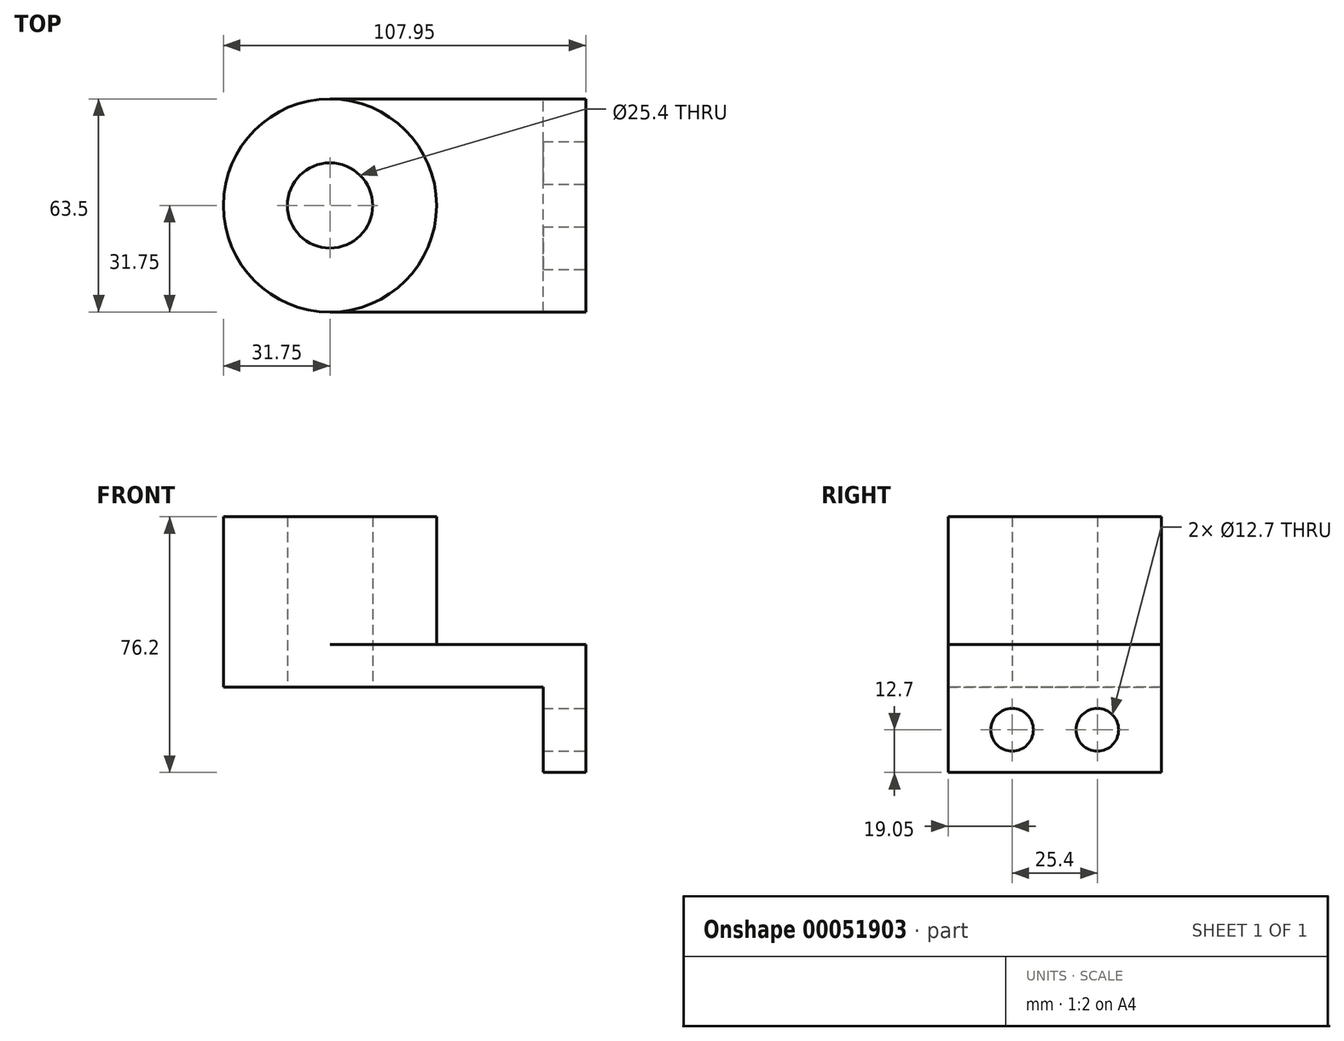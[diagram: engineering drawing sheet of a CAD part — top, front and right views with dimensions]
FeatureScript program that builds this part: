
annotation { "Feature Type Name" : "Feature", "Feature Type Description" : "" }
export const myFeature = defineFeature(function(context is Context, id is Id, definition is map)
    precondition{}
    {
        {
            var Q0;
            Q0=qCreatedBy(makeId("Top.planeOp"),FACE);
            var sketch = newSketch(context, id + "F0", { "sketchPlane" : qUnion([Q0])});
            skLineSegment(sketch, "E0.rect.bottom", {"start": v(38.1, -31.75) * mm, "end": v(-38.1, -31.75) * mm});
            skLineSegment(sketch, "E0.rect.top", {"start": v(38.1, 31.75) * mm, "end": v(-38.1, 31.75) * mm});
            skLineSegment(sketch, "E0.rect.left", {"start": v(38.1, -31.75) * mm, "end": v(38.1, 31.75) * mm});
            skLineSegment(sketch, "E0.rect.right", {"start": v(-38.1, -31.75) * mm, "end": v(-38.1, 31.75) * mm});
            skPoint(sketch, "E0.rect.middle", {"position": v(0, 0) * mm});
            skCircle(sketch, "E1", {"center": v(-38.1, 0) * mm, "radius": 31.75 * mm});
            skCircle(sketch, "E2", {"center": v(-38.1, 0) * mm, "radius": 12.7 * mm});
            skSolve(sketch);
        }
        {
            var Q0;
            Q0 = qSketchRegion(id + "F0", true);
            extrude(context, id + "F1", {"entities" : qUnion([Q0]), "depth" : 12.7 * mm});
        }
        {
            var Q0;
            {var subQ1=sQuery(id+"F0.wireOp",EDGE,"E0.rect.right");var subQ3=sQuery(id+"F0.wireOp",EDGE,"E2");var subQ4=makeQuery(id+"F0.imprint","INTERSECT",VERTEX,{"disambiguationData":[OD(0.0)],"derivedFrom":[subQ1,subQ3]});Q0=makeQuery(id+"F0.imprint","IMPRINT",FACE,{"disambiguationData":[TD([[makeQuery(id+"F0.imprint","IMPRINT",EDGE,{"disambiguationData":[TD([[subQ4,1.0]])],"derivedFrom":subQ3}),-1.0]])]});}
            var Q1;
            {var subQ1=sQuery(id+"F0.wireOp",EDGE,"E0.rect.right");var subQ3=sQuery(id+"F0.wireOp",EDGE,"E2");var subQ4=makeQuery(id+"F0.imprint","INTERSECT",VERTEX,{"disambiguationData":[OD(0.0)],"derivedFrom":[subQ1,subQ3]});Q1=makeQuery(id+"F0.imprint","IMPRINT",FACE,{"disambiguationData":[TD([[makeQuery(id+"F0.imprint","IMPRINT",EDGE,{"disambiguationData":[TD([[subQ4,-1.0]])],"derivedFrom":subQ3}),-1.0]])]});}
            extrude(context, id + "F2", {"entities" : qUnion([Q0, Q1]), "operationType" : NewBodyOperationType.ADD, "depth" : 50.8 * mm});
        }
        {
            var Q0;
            Q0=makeQuery(id+"F1.opExtrude","SWEPT_FACE",FACE,{"disambiguationData":[OSD([sQuery(id+"F0.wireOp",EDGE,"E0.rect.left")])]});
            var sketch = newSketch(context, id + "F3", { "sketchPlane" : qUnion([Q0])});
            skLineSegment(sketch, "E3.bottom", {"start": v(-31.75, 12.7) * mm, "end": v(31.75, 12.7) * mm});
            skLineSegment(sketch, "E3.top", {"start": v(-31.75, -25.4) * mm, "end": v(31.75, -25.4) * mm});
            skLineSegment(sketch, "E3.left", {"start": v(-31.75, 12.7) * mm, "end": v(-31.75, -25.4) * mm});
            skLineSegment(sketch, "E3.right", {"start": v(31.75, 12.7) * mm, "end": v(31.75, -25.4) * mm});
            skCircle(sketch, "E4", {"center": v(-12.7, -12.7) * mm, "radius": 6.35 * mm});
            skLineSegment(sketch, "E5", {"start": v(0, 0) * mm, "end": v(0, -25.4) * mm});
            skCircle(sketch, "E6.MirrorC", {"center": v(12.7, -12.7) * mm, "radius": 6.35 * mm});
            skSolve(sketch);
        }
        {
            var Q0;
            {var subQ6=sQuery(id+"F3.wireOp",EDGE,"E3.bottom");Q0=makeQuery(id+"F3.imprint","IMPRINT",FACE,{"disambiguationData":[TD([[makeQuery(id+"F3.imprint","IMPRINT",EDGE,{"derivedFrom":subQ6}),-1.0]])]});}
            var Q1;
            Q1=makeQuery(id+"F3.imprint","IMPRINT",FACE,{"disambiguationData":[TD([[makeQuery(id+"F3.imprint","IMPRINT",EDGE,{"derivedFrom":sQuery(id+"F3.wireOp",EDGE,"E4")}),-1.0]])]});
            var Q2;
            {var subQ0=sQuery(id+"F3.wireOp",EDGE,"E5");Q2=makeQuery(id+"F3.imprint","IMPRINT",FACE,{"disambiguationData":[TD([[makeQuery(id+"F3.imprint","IMPRINT",EDGE,{"derivedFrom":subQ0}),1.0]])]});}
            extrude(context, id + "F4", {"entities" : qUnion([Q0, Q1, Q2]), "operationType" : NewBodyOperationType.ADD, "oppositeDirection" : true, "depth" : 12.7 * mm});
        }
    });
